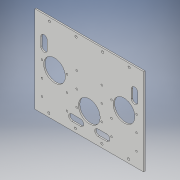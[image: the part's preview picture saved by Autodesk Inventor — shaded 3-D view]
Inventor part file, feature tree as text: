
AUTODESK INVENTOR PART (.ipt)
format: ipt  version: 2019 (Build 230136000, 136)  size: 232,448 bytes
history: native  units: mm
features: extrude x4, sketch x1, mirror x1
ambient origin geometry x8: Origin, YZ Plane, XZ Plane, XY Plane, X Axis, Y Axis, Z Axis, Center Point
bodies: Solid1 (feature_tree)
feature tree (6):
  sketch  "Sketch1"  dims[d0=150.0mm d1=120.0mm d2=60.0mm d3=60.0mm d5=27.0mm d6=27.0mm d7=5.0mm d8=20.0mm d9=30.0mm d12=2.0mm d13=0.0mm d14=20.0mm d15=36.666667mm d16=36.666667mm d17=3.2mm d18=3.2mm d19=3.2mm d20=3.2mm d21=3.2mm d22=3.2mm d23=3.2mm d24=3.2mm d25=4.0mm d26=17.3mm d27=17.3mm d28=44.0mm d29=2.5mm d30=2.5mm d31=2.5mm d32=2.5mm d33=10.0mm d34=0.0mm d40=40.0mm d41=30.0mm d42=4.0mm d43=17.3mm d44=17.3mm d45=44.0mm d46=2.5mm d47=2.5mm d48=2.5mm d49=2.5mm d50=40.0mm d51=30.0mm d52=4.0mm d53=17.3mm d54=17.3mm d55=44.0mm d56=2.5mm d57=2.5mm d58=2.5mm d59=2.5mm d60=40.0mm d67=6.0mm d68=6.0mm d69=12.5mm d70=25.0mm d71=1.5mm d72=10.0mm d73=0.0mm d80=12.0mm d81=9.0mm d82=6.0mm d83=12.0mm d84=10.0mm d85=0.0mm d86=2.5mm d87=2.5mm d88=2.5mm d89=2.5mm d90=22.0mm d94=2.5mm d95=22.0mm d96=2.5mm]
  extrude  "Extrusion1"  Depth=120.0mm
  extrude  "Extrusion2"  Depth=10.0mm
  extrude  "Extrusion3"  Depth=10.0mm
  extrude  "Extrusion4"  Depth=10.0mm
  mirror  "Mirror1"
